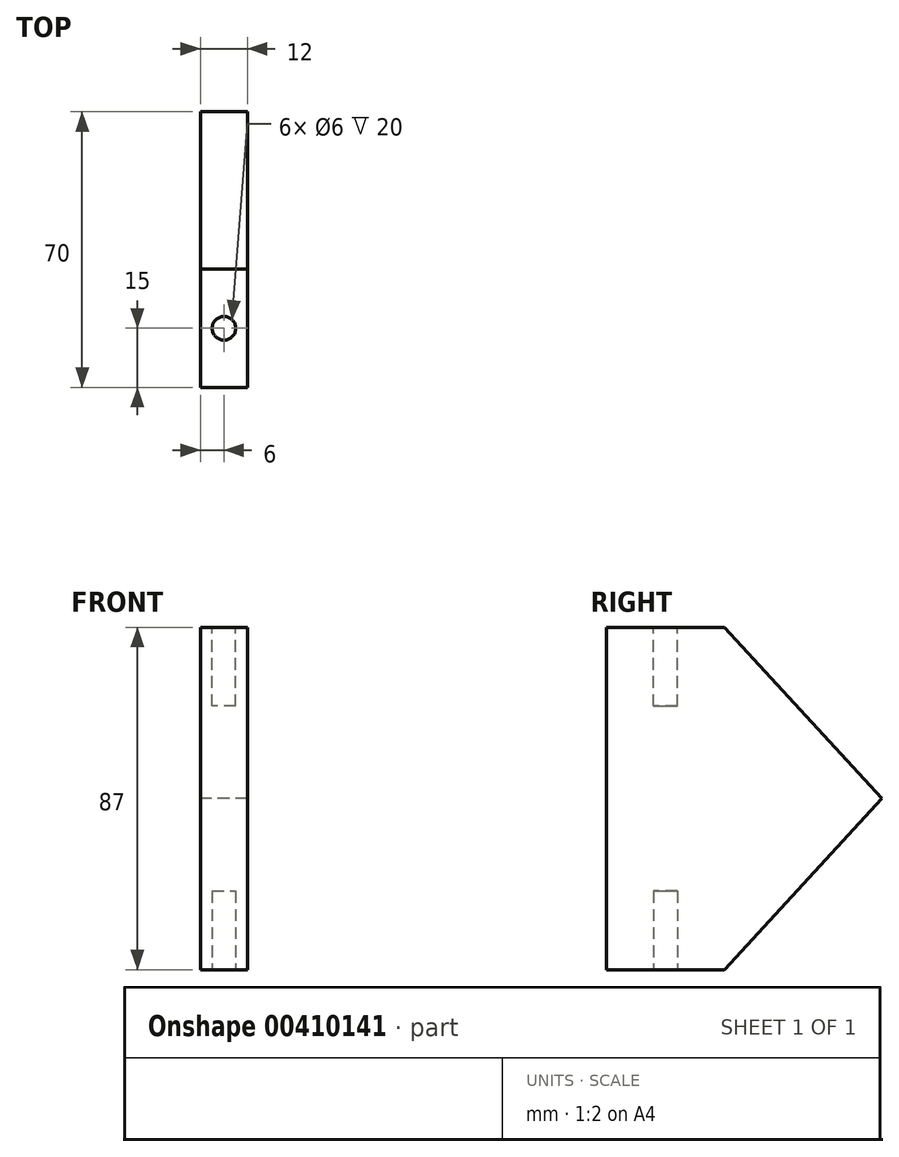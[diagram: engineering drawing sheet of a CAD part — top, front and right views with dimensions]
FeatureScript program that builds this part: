
annotation { "Feature Type Name" : "Feature", "Feature Type Description" : "" }
export const myFeature = defineFeature(function(context is Context, id is Id, definition is map)
    precondition{}
    {
        {
            var Q0;
            Q0=qCreatedBy(makeId("Right.planeOp"),FACE);
            var sketch = newSketch(context, id + "F0", { "sketchPlane" : qUnion([Q0])});
            skLineSegment(sketch, "E0.bottom", {"start": v(0, 0) * mm, "end": v(60, 0) * mm});
            skLineSegment(sketch, "E0.top", {"start": v(0, 87) * mm, "end": v(60, 87) * mm});
            skLineSegment(sketch, "E0.left", {"start": v(0, 0) * mm, "end": v(0, 87) * mm});
            skLineSegment(sketch, "E0.right", {"start": v(60, 0) * mm, "end": v(60, 87) * mm, "construction": true});
            skLineSegment(sketch, "E1", {"start": v(-42.15, 43.5) * mm, "end": v(100, 43.5) * mm, "construction": true});
            skPoint(sketch, "E2", {"position": v(0, 43.5) * mm});
            skPoint(sketch, "E3", {"position": v(60, 43.5) * mm});
            skLineSegment(sketch, "E4", {"start": v(60, 0) * mm, "end": v(100, 43.5) * mm});
            skLineSegment(sketch, "E5", {"start": v(100, 43.5) * mm, "end": v(60, 87) * mm});
            skSolve(sketch);
        }
        {
            var Q0;
            Q0=qSketchRegion(id+"F0",true);
            extrude(context, id + "F1", {"entities" : qUnion([Q0]), "depth" : 12 * mm});
        }
        {
            var Q0;
            Q0=makeQuery(id+"F1.opExtrude","SWEPT_FACE",FACE,{"disambiguationData":[OSD([sQuery(id+"F0.wireOp",EDGE,"E0.top")])]});
            var sketch = newSketch(context, id + "F2", { "sketchPlane" : qUnion([Q0])});
            skLineSegment(sketch, "E6", {"start": v(6, 0) * mm, "end": v(6, 60) * mm, "construction": true});
            skCircle(sketch, "E7", {"center": v(6, 45) * mm, "radius": 3 * mm});
            skCircle(sketch, "E8.0.1.0", {"center": v(6, 15) * mm, "radius": 3 * mm});
            skCircle(sketch, "E8.0.2.0", {"center": v(6, -15) * mm, "radius": 3 * mm});
            skLineSegment(sketch, "E8.direction1", {"start": v(6, 45) * mm, "end": v(31, 45) * mm, "construction": true});
            skLineSegment(sketch, "E8.direction2", {"start": v(6, 45) * mm, "end": v(6, 15) * mm, "construction": true});
            skSolve(sketch);
        }
        {
            var Q0;
            Q0 = qSketchRegion(id + "F2", true);
            extrude(context, id + "F3", {"entities" : qUnion([Q0]), "operationType" : NewBodyOperationType.REMOVE, "oppositeDirection" : true, "depth" : 20 * mm});
        }
        {
            var Q0;
            Q0=makeQuery(id+"F1.opExtrude","SWEPT_FACE",FACE,{"disambiguationData":[OSD([sQuery(id+"F0.wireOp",EDGE,"E0.bottom")])]});
            var sketch = newSketch(context, id + "F4", { "sketchPlane" : qUnion([Q0])});
            skLineSegment(sketch, "E9.0", {"start": v(6, 0) * mm, "end": v(6, -60) * mm});
            skCircle(sketch, "E9.1", {"center": v(6, -45) * mm, "radius": 3 * mm});
            skCircle(sketch, "E9.2", {"center": v(6, -15) * mm, "radius": 3 * mm});
            skCircle(sketch, "E9.3", {"center": v(6, 15) * mm, "radius": 3 * mm});
            skLineSegment(sketch, "E9.4", {"start": v(6, -45) * mm, "end": v(31, -45) * mm});
            skLineSegment(sketch, "E9.5", {"start": v(6, -45) * mm, "end": v(6, -15) * mm});
            skSolve(sketch);
        }
        {
            var Q0;
            Q0 = qSketchRegion(id + "F4", true);
            extrude(context, id + "F5", {"entities" : qUnion([Q0]), "operationType" : NewBodyOperationType.REMOVE, "oppositeDirection" : true, "depth" : 20 * mm});
        }
        {
            var Q0;
            Q0=makeQuery(id+"F1.opExtrude","CAP_FACE",FACE,{"disambiguationData":[OSD([sQuery(id+"F0.wireOp",EDGE,"E0.bottom"),sQuery(id+"F0.wireOp",EDGE,"E0.top"),sQuery(id+"F0.wireOp",EDGE,"E0.left"),sQuery(id+"F0.wireOp",EDGE,"E4"),sQuery(id+"F0.wireOp",EDGE,"E5")])],"isStart":false});
            var sketch = newSketch(context, id + "F6", { "sketchPlane" : qUnion([Q0])});
            skLineSegment(sketch, "E10.bottom", {"start": v(0, 0) * mm, "end": v(30, 0) * mm});
            skLineSegment(sketch, "E10.top", {"start": v(0, 87) * mm, "end": v(30, 87) * mm});
            skLineSegment(sketch, "E10.left", {"start": v(0, 0) * mm, "end": v(0, 87) * mm});
            skLineSegment(sketch, "E10.right", {"start": v(30, 0) * mm, "end": v(30, 87) * mm});
            skSolve(sketch);
        }
        {
            var Q0;
            Q0 = qSketchRegion(id + "F6", true);
            extrude(context, id + "F7", {"entities" : qUnion([Q0]), "operationType" : NewBodyOperationType.REMOVE, "oppositeDirection" : true, "depth" : 25 * mm, "offsetDistance" : 25 * mm});
        }
    });
